# Revit family: CRU
name_source: partatom
category: Lighting Fixtures
units: mm (PartAtom-declared; Revit-internal decimal feet)

## family parameters
Cut with Voids When Loaded = No
Host = Face
Light Source = No
OmniClass Number = 23.80.70.11.14.17
OmniClass Title = Direct/Indirect
Part Type = Normal
Room Calculation Point = No
Round Connector Dimension = Use Diameter
Shared = Yes

## types (1)
- CRU
    Apparent Load = 0 VA
    Assembly Code = D5020200
    Default Elevation = 1219 mm
    Description = The CRU is a Damp Location Listed, City of Chicago Approved Steel Recessed Unit.
    Glass = Glass -  White
    Housing Material = Paint - Matte White
    Indicator Bulb = Paint -  Red
    Lamp = Halogen Lamp
    Load Classification = Lighting
    Manufacturer = Dual-Lite
    Model = Chicago Recessed Unit
    Mounting = Ceiling
    Power Factor = 1
    Switch = Paint -  Textured Camera Black
    Type Comments = Lighting Fixture
    URL = https://www.currentlighting.com
    Voltage = 120 V
    Warranty = 5-Years Warranty
    Wattage Comments = 12W

## geometry (parser evidence)
native form markers: Sweep x6
no freeform markers — native parametric forms only
